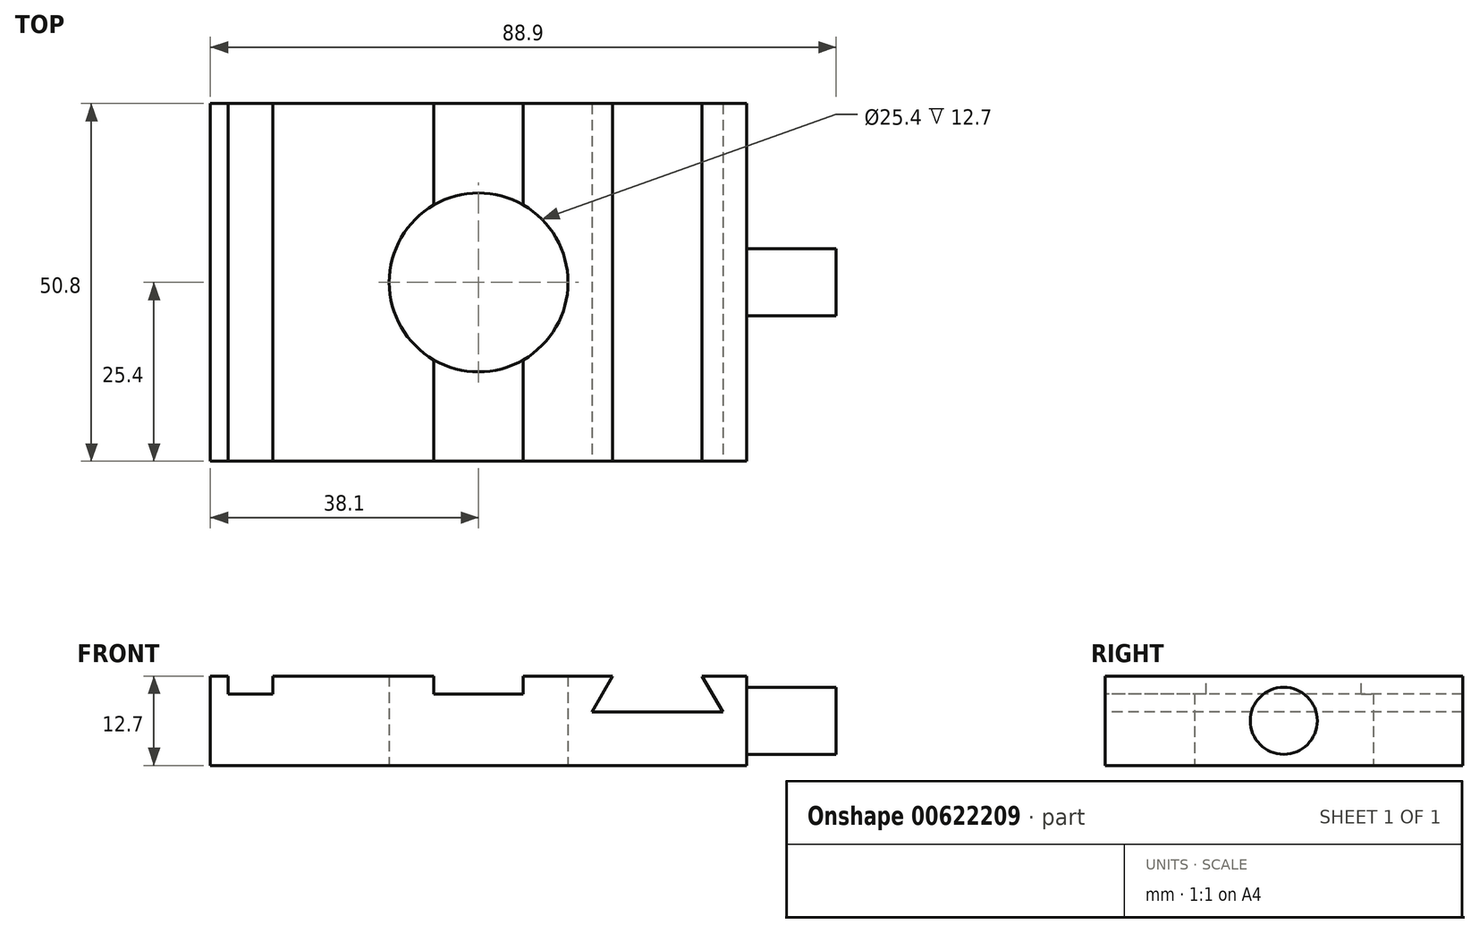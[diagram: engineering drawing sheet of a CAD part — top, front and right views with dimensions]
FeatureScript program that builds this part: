
annotation { "Feature Type Name" : "Feature", "Feature Type Description" : "" }
export const myFeature = defineFeature(function(context is Context, id is Id, definition is map)
    precondition{}
    {
        {
            var Q0;
            Q0=qCreatedBy(makeId("Top.planeOp"),FACE);
            var sketch = newSketch(context, id + "F0", { "sketchPlane" : qUnion([Q0])});
            skLineSegment(sketch, "E0.bottom", {"start": v(38.1, -25.4) * mm, "end": v(-38.1, -25.4) * mm});
            skLineSegment(sketch, "E0.top", {"start": v(38.1, 25.4) * mm, "end": v(-38.1, 25.4) * mm});
            skLineSegment(sketch, "E0.left", {"start": v(38.1, -25.4) * mm, "end": v(38.1, 25.4) * mm});
            skLineSegment(sketch, "E0.right", {"start": v(-38.1, -25.4) * mm, "end": v(-38.1, 25.4) * mm});
            skPoint(sketch, "E0.middle", {"position": v(0, 0) * mm});
            skCircle(sketch, "E1", {"center": v(0, 0) * mm, "radius": 12.7 * mm});
            skSolve(sketch);
        }
        {
            var Q0;
            Q0=makeQuery(id+"F0.imprint","IMPRINT",FACE,{"disambiguationData":[TD([[makeQuery(id+"F0.imprint","IMPRINT",EDGE,{"derivedFrom":sQuery(id+"F0.wireOp",EDGE,"E0.bottom")}),-1.0]])]});
            extrude(context, id + "F1", {"entities" : qUnion([Q0]), "depth" : 12.7 * mm, "offsetDistance" : 25.4 * mm});
        }
        {
            var Q0;
            Q0=makeQuery(id+"F1.opExtrude","CAP_FACE",FACE,{"disambiguationData":[OSD([sQuery(id+"F0.wireOp",EDGE,"E0.bottom"),sQuery(id+"F0.wireOp",EDGE,"E0.top"),sQuery(id+"F0.wireOp",EDGE,"E0.left"),sQuery(id+"F0.wireOp",EDGE,"E0.right"),sQuery(id+"F0.wireOp",EDGE,"E1")])],"isStart":false});
            var sketch = newSketch(context, id + "F2", { "sketchPlane" : qUnion([Q0])});
            skLineSegment(sketch, "E2.bottom", {"start": v(-35.56, 25.4) * mm, "end": v(-29.21, 25.4) * mm});
            skLineSegment(sketch, "E2.top", {"start": v(-35.56, -25.4) * mm, "end": v(-29.21, -25.4) * mm});
            skLineSegment(sketch, "E2.left", {"start": v(-35.56, 25.4) * mm, "end": v(-35.56, -25.4) * mm});
            skLineSegment(sketch, "E2.right", {"start": v(-29.21, 25.4) * mm, "end": v(-29.21, -25.4) * mm});
            skLineSegment(sketch, "E3", {"start": v(-6.35, 25.4) * mm, "end": v(-6.35, -25.4) * mm});
            skLineSegment(sketch, "E4", {"start": v(-6.35, -25.4) * mm, "end": v(6.35, -25.4) * mm});
            skLineSegment(sketch, "E5", {"start": v(6.35, -25.4) * mm, "end": v(6.35, 25.4) * mm});
            skLineSegment(sketch, "E6", {"start": v(6.35, 25.4) * mm, "end": v(-6.35, 25.4) * mm});
            skLineSegment(sketch, "E7", {"start": v(0, 25.4) * mm, "end": v(0, -25.4) * mm, "construction": true});
            skSolve(sketch);
        }
        {
            var Q0;
            Q0=makeQuery(id+"F2.imprint","IMPRINT",FACE,{"disambiguationData":[TD([[makeQuery(id+"F2.imprint","IMPRINT",EDGE,{"derivedFrom":sQuery(id+"F2.wireOp",EDGE,"E2.bottom")}),1.0]])]});
            var Q1;
            {var subQ0=sQuery(id+"F2.wireOp",EDGE,"E4");Q1=makeQuery(id+"F2.imprint","IMPRINT",FACE,{"disambiguationData":[TD([[makeQuery(id+"F2.imprint","IMPRINT",EDGE,{"derivedFrom":subQ0}),-1.0]])]});}
            var Q2;
            {var subQ0=sQuery(id+"F2.wireOp",EDGE,"E6");Q2=makeQuery(id+"F2.imprint","IMPRINT",FACE,{"disambiguationData":[TD([[makeQuery(id+"F2.imprint","IMPRINT",EDGE,{"derivedFrom":subQ0}),1.0]])]});}
            extrude(context, id + "F3", {"entities" : qUnion([Q0, Q1, Q2]), "operationType" : NewBodyOperationType.REMOVE, "oppositeDirection" : true, "depth" : 2.54 * mm, "offsetDistance" : 25.4 * mm});
        }
        {
            var Q0;
            Q0=makeQuery(id+"F1.opExtrude","SWEPT_FACE",FACE,{"disambiguationData":[OSD([sQuery(id+"F0.wireOp",EDGE,"E0.bottom")])]});
            var sketch = newSketch(context, id + "F4", { "sketchPlane" : qUnion([Q0])});
            skLineSegment(sketch, "E8", {"start": v(19.05, 12.7) * mm, "end": v(16.12, 7.62) * mm});
            skLineSegment(sketch, "E9", {"start": v(16.12, 7.62) * mm, "end": v(34.68, 7.62) * mm});
            skLineSegment(sketch, "E10", {"start": v(34.68, 7.62) * mm, "end": v(31.75, 12.7) * mm});
            skLineSegment(sketch, "E11", {"start": v(25.4, 7.62) * mm, "end": v(25.4, 12.7) * mm, "construction": true});
            skSolve(sketch);
        }
        {
            var Q0;
            {var subQ0=sQuery(id+"F4.wireOp",EDGE,"E8");Q0=makeQuery(id+"F4.imprint","IMPRINT",FACE,{"disambiguationData":[TD([[makeQuery(id+"F4.imprint","IMPRINT",EDGE,{"derivedFrom":subQ0}),1.0]])]});}
            extrude(context, id + "F5", {"entities" : qUnion([Q0]), "operationType" : NewBodyOperationType.REMOVE, "endBound" : BoundingType.THROUGH_ALL, "oppositeDirection" : true, "depth" : 25.4 * mm, "offsetDistance" : 25.4 * mm});
        }
        {
            var Q0;
            Q0=makeQuery(id+"F1.opExtrude","SWEPT_FACE",FACE,{"disambiguationData":[OSD([sQuery(id+"F0.wireOp",EDGE,"E0.left")])]});
            var sketch = newSketch(context, id + "F6", { "sketchPlane" : qUnion([Q0])});
            skCircle(sketch, "E12", {"center": v(0, 6.35) * mm, "radius": 4.76 * mm});
            skPoint(sketch, "E12.centerSnap0", {"position": v(-25.4, 6.35) * mm});
            skPoint(sketch, "E12.centerSnap1", {"position": v(0, 12.7) * mm});
            skSolve(sketch);
        }
        {
            var Q0;
            Q0=makeQuery(id+"F6.imprint","IMPRINT",FACE,{"disambiguationData":[TD([[makeQuery(id+"F6.imprint","IMPRINT",EDGE,{"derivedFrom":sQuery(id+"F6.wireOp",EDGE,"E12")}),1.0]])]});
            extrude(context, id + "F7", {"entities" : qUnion([Q0]), "operationType" : NewBodyOperationType.ADD, "depth" : 12.7 * mm, "offsetDistance" : 25.4 * mm});
        }
    });
